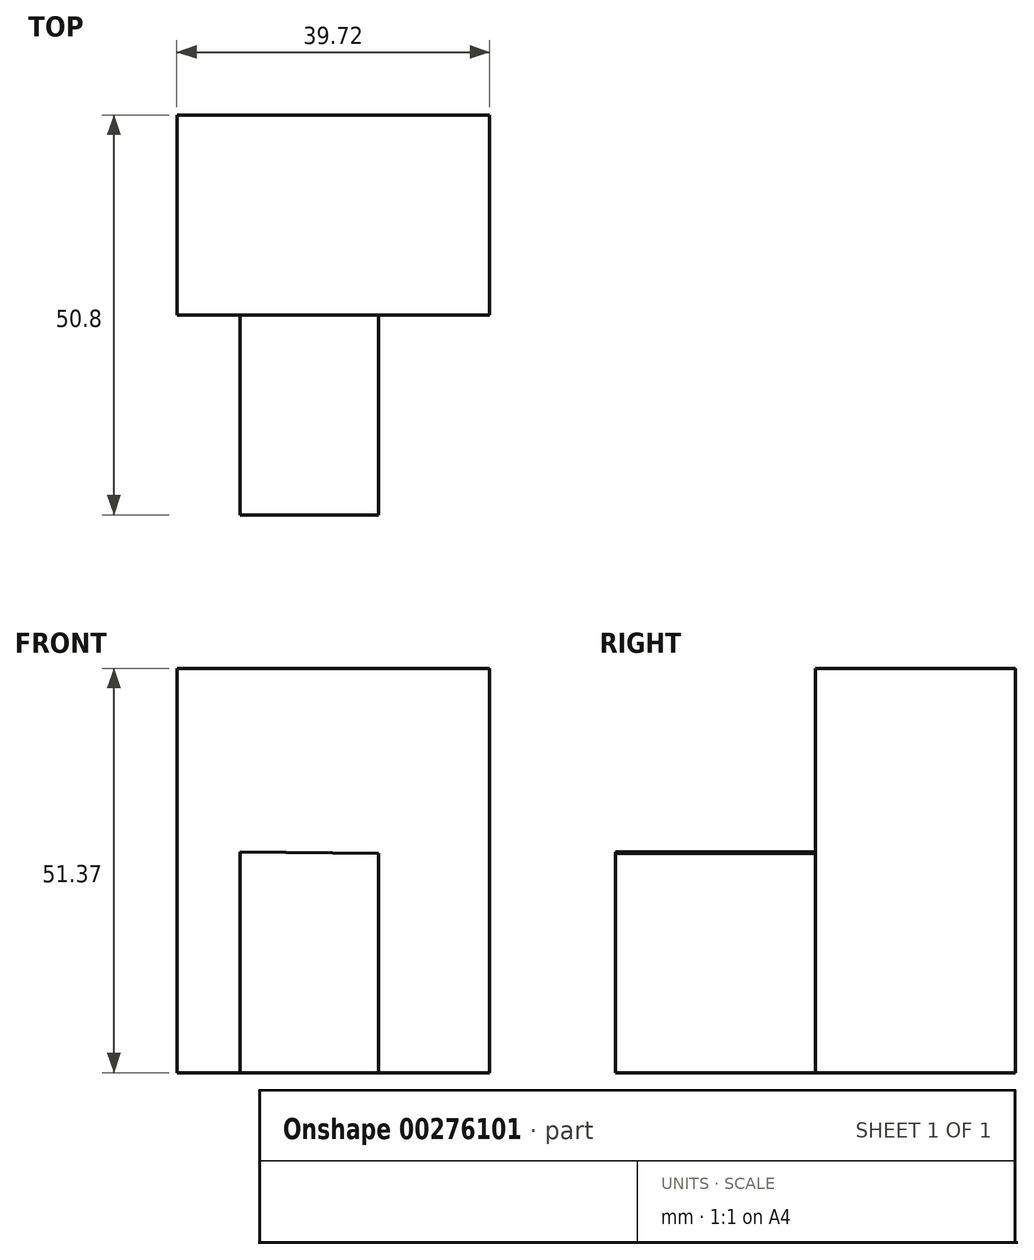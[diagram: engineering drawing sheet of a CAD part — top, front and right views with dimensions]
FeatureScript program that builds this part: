
annotation { "Feature Type Name" : "Feature", "Feature Type Description" : "" }
export const myFeature = defineFeature(function(context is Context, id is Id, definition is map)
    precondition{}
    {
        {
            var Q0;
            Q0=qCreatedBy(makeId("Front.planeOp"),FACE);
            var sketch = newSketch(context, id + "F0", { "sketchPlane" : qUnion([Q0])});
            skLineSegment(sketch, "E0", {"start": v(-51.18, 51.37) * mm, "end": v(-51.18, 0) * mm});
            skLineSegment(sketch, "E1", {"start": v(-11.46, 0) * mm, "end": v(-11.46, 51.37) * mm});
            skLineSegment(sketch, "E2", {"start": v(-51.18, 51.37) * mm, "end": v(-11.46, 51.37) * mm});
            skLineSegment(sketch, "E3", {"start": v(-51.18, 0) * mm, "end": v(-11.46, 0) * mm});
            skSolve(sketch);
        }
        {
            var Q0;
            Q0 = qSketchRegion(id + "F0", true);
            extrude(context, id + "F1", {"entities" : qUnion([Q0]), "depth" : 25.4 * mm});
        }
        {
            var Q0;
            Q0=makeQuery(id+"F1.opExtrude","CAP_FACE",FACE,{"disambiguationData":[OSD([sQuery(id+"F0.wireOp",EDGE,"E0"),sQuery(id+"F0.wireOp",EDGE,"E1"),sQuery(id+"F0.wireOp",EDGE,"E2"),sQuery(id+"F0.wireOp",EDGE,"E3")])],"isStart":false});
            var sketch = newSketch(context, id + "F2", { "sketchPlane" : qUnion([Q0])});
            skLineSegment(sketch, "E4", {"start": v(-43.16, 28.07) * mm, "end": v(-43.16, 0) * mm});
            skLineSegment(sketch, "E5", {"start": v(-25.59, 0) * mm, "end": v(-25.59, 27.88) * mm});
            skLineSegment(sketch, "E6", {"start": v(-43.16, 28.07) * mm, "end": v(-25.59, 27.88) * mm});
            skSolve(sketch);
        }
        {
            var Q0;
            {var subQ0=sQuery(id+"F2.wireOp",EDGE,"E4");Q0=makeQuery(id+"F2.imprint","IMPRINT",FACE,{"disambiguationData":[TD([[makeQuery(id+"F2.imprint","IMPRINT",EDGE,{"derivedFrom":subQ0}),1.0]])]});}
            extrude(context, id + "F3", {"entities" : qUnion([Q0]), "operationType" : NewBodyOperationType.ADD, "depth" : 25.4 * mm});
        }
    });
